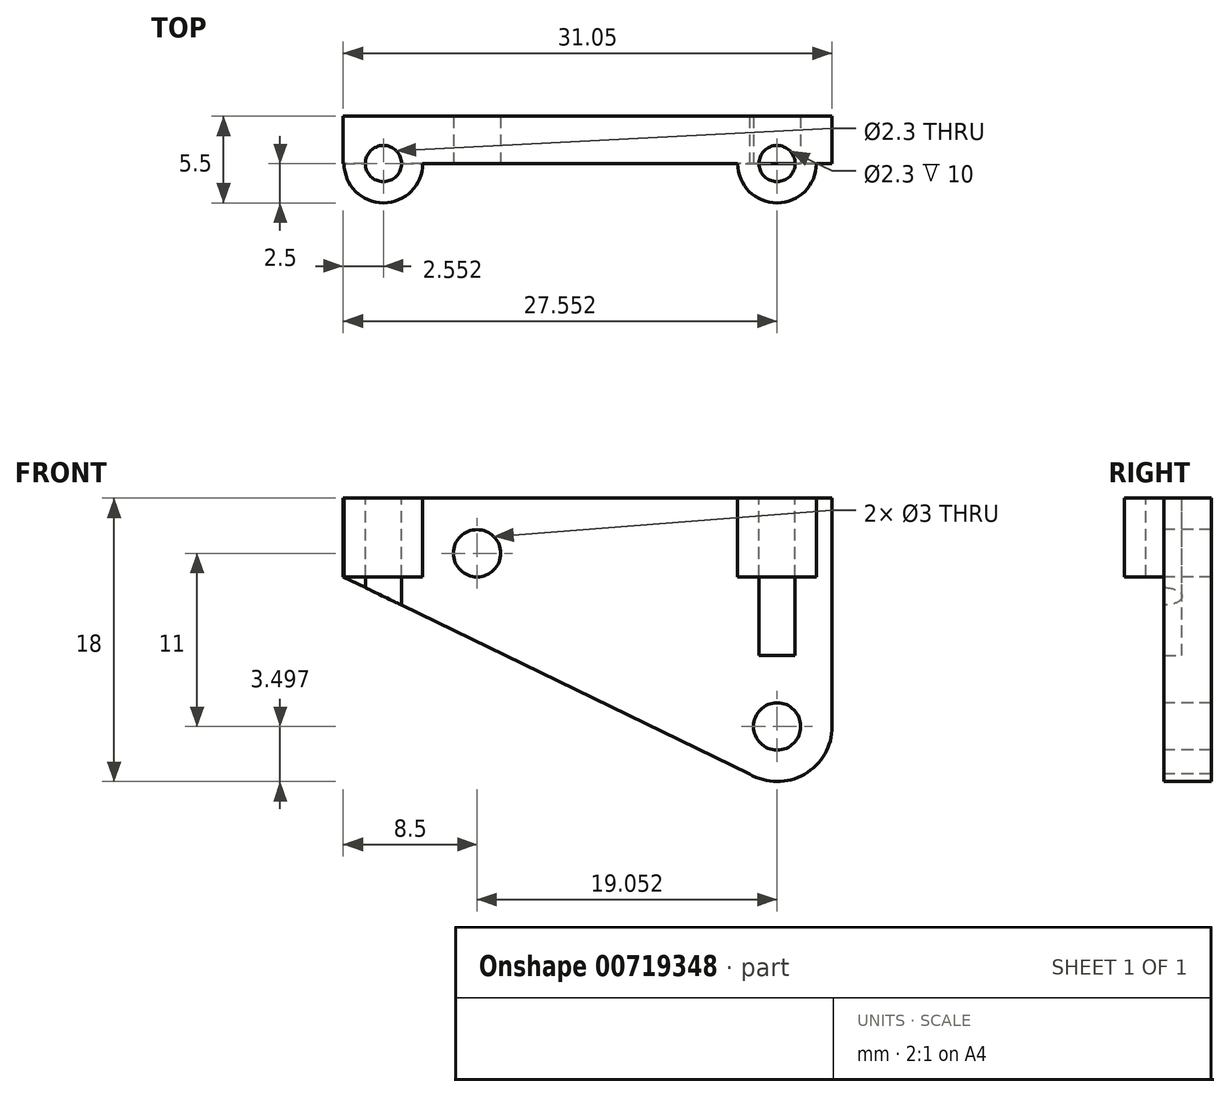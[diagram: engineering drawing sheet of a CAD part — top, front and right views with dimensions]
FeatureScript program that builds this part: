
annotation { "Feature Type Name" : "Feature", "Feature Type Description" : "" }
export const myFeature = defineFeature(function(context is Context, id is Id, definition is map)
    precondition{}
    {
        {
            var Q0;
            Q0=qCreatedBy(makeId("Front.planeOp"),FACE);
            var sketch = newSketch(context, id + "F0", { "sketchPlane" : qUnion([Q0])});
            skCircle(sketch, "E0", {"center": v(-7.35, 20.59) * mm, "radius": 1.5 * mm});
            skArc(sketch, "E1", {"start": v(10.4, 10.34) * mm, "mid": v(10.95, 8.29) * mm, "end": v(13, 8.84) * mm});
            skCircle(sketch, "E2", {"center": v(11.7, 9.59) * mm, "radius": 1.5 * mm});
            skArc(sketch, "E3", {"start": v(9.94, 6.56) * mm, "mid": v(13.45, 6.55) * mm, "end": v(15.2, 9.59) * mm});
            skLineSegment(sketch, "E4", {"start": v(15.2, 9.59) * mm, "end": v(15.2, 24.09) * mm});
            skLineSegment(sketch, "E5", {"start": v(-10.85, 24.09) * mm, "end": v(15.2, 24.09) * mm});
            skLineSegment(sketch, "E6", {"start": v(-10.85, 24.09) * mm, "end": v(-15.85, 24.09) * mm});
            skLineSegment(sketch, "E7", {"start": v(-15.85, 24.09) * mm, "end": v(-15.85, 19.09) * mm});
            skLineSegment(sketch, "E8", {"start": v(-15.85, 19.09) * mm, "end": v(9.94, 6.56) * mm});
            skSolve(sketch);
        }
        {
            var Q0;
            Q0=makeQuery(id+"F0.imprint","IMPRINT",FACE,{"disambiguationData":[TD([[makeQuery(id+"F0.imprint","IMPRINT",EDGE,{"derivedFrom":sQuery(id+"F0.wireOp",EDGE,"E0")}),-1.0]])]});
            extrude(context, id + "F1", {"entities" : qUnion([Q0]), "depth" : 3 * mm, "offsetDistance" : 25 * mm});
        }
        {
            var Q0;
            Q0=makeQuery(id+"F1.opExtrude","SWEPT_FACE",FACE,{"disambiguationData":[OSD([sQuery(id+"F0.wireOp",EDGE,"E5")])]});
            var sketch = newSketch(context, id + "F2", { "sketchPlane" : qUnion([Q0])});
            skCircle(sketch, "E9", {"center": v(11.7, 0) * mm, "radius": 2.5 * mm});
            skCircle(sketch, "E10", {"center": v(-13.3, 0) * mm, "radius": 2.5 * mm});
            skSolve(sketch);
        }
        {
            var Q0;
            Q0=qSketchRegion(id+"F2",true);
            extrude(context, id + "F3", {"entities" : qUnion([Q0]), "operationType" : NewBodyOperationType.ADD, "oppositeDirection" : true, "depth" : 5 * mm, "offsetDistance" : 25 * mm});
        }
        {
            var Q0;
            Q0=makeQuery(id+"F3.boolean.opBoolean","MERGE",FACE,{"derivedFrom":[makeQuery(id+"F1.opExtrude","SWEPT_FACE",FACE,{"disambiguationData":[OSD([sQuery(id+"F0.wireOp",EDGE,"E5")])]}),makeQuery(id+"F3.opExtrude","CAP_FACE",FACE,{"disambiguationData":[OSD([sQuery(id+"F2.wireOp",EDGE,"E9")])],"isStart":true}),makeQuery(id+"F3.opExtrude","CAP_FACE",FACE,{"disambiguationData":[OSD([sQuery(id+"F2.wireOp",EDGE,"E10")])],"isStart":true})]});
            var sketch = newSketch(context, id + "F4", { "sketchPlane" : qUnion([Q0])});
            skCircle(sketch, "E11", {"center": v(11.7, 0) * mm, "radius": 1.15 * mm});
            skCircle(sketch, "E12", {"center": v(-13.3, 0) * mm, "radius": 1.15 * mm});
            skSolve(sketch);
        }
        {
            var Q0;
            Q0=qSketchRegion(id+"F4",true);
            extrude(context, id + "F5", {"entities" : qUnion([Q0]), "operationType" : NewBodyOperationType.REMOVE, "oppositeDirection" : true, "depth" : 10 * mm, "offsetDistance" : 25 * mm});
        }
        {
            var Q0;
            Q0=makeQuery(id+"F1.opExtrude","SWEPT_BODY",BODY,{"disambiguationData":[OSD([sQuery(id+"F0.wireOp",EDGE,"E0"),sQuery(id+"F0.wireOp",EDGE,"E2"),sQuery(id+"F0.wireOp",EDGE,"E3"),sQuery(id+"F0.wireOp",EDGE,"E4"),sQuery(id+"F0.wireOp",EDGE,"E5"),sQuery(id+"F0.wireOp",EDGE,"E6"),sQuery(id+"F0.wireOp",EDGE,"E7"),sQuery(id+"F0.wireOp",EDGE,"E8")])]});
            var Q1;
            Q1=qCreatedBy(makeId("Front.planeOp"),FACE);
            mirror(context, id + "F6", {"entities" : qUnion([Q0]), "mirrorPlane" : qUnion([Q1])});
        }
        {
            var Q0;
            Q0=makeQuery(id+"F1.opExtrude","SWEPT_BODY",BODY,{"disambiguationData":[OSD([sQuery(id+"F0.wireOp",EDGE,"E0"),sQuery(id+"F0.wireOp",EDGE,"E2"),sQuery(id+"F0.wireOp",EDGE,"E3"),sQuery(id+"F0.wireOp",EDGE,"E4"),sQuery(id+"F0.wireOp",EDGE,"E5"),sQuery(id+"F0.wireOp",EDGE,"E6"),sQuery(id+"F0.wireOp",EDGE,"E7"),sQuery(id+"F0.wireOp",EDGE,"E8")])]});
            deleteBodies(context, id + "F7", {"entities" : qUnion([Q0])});
        }
    });
